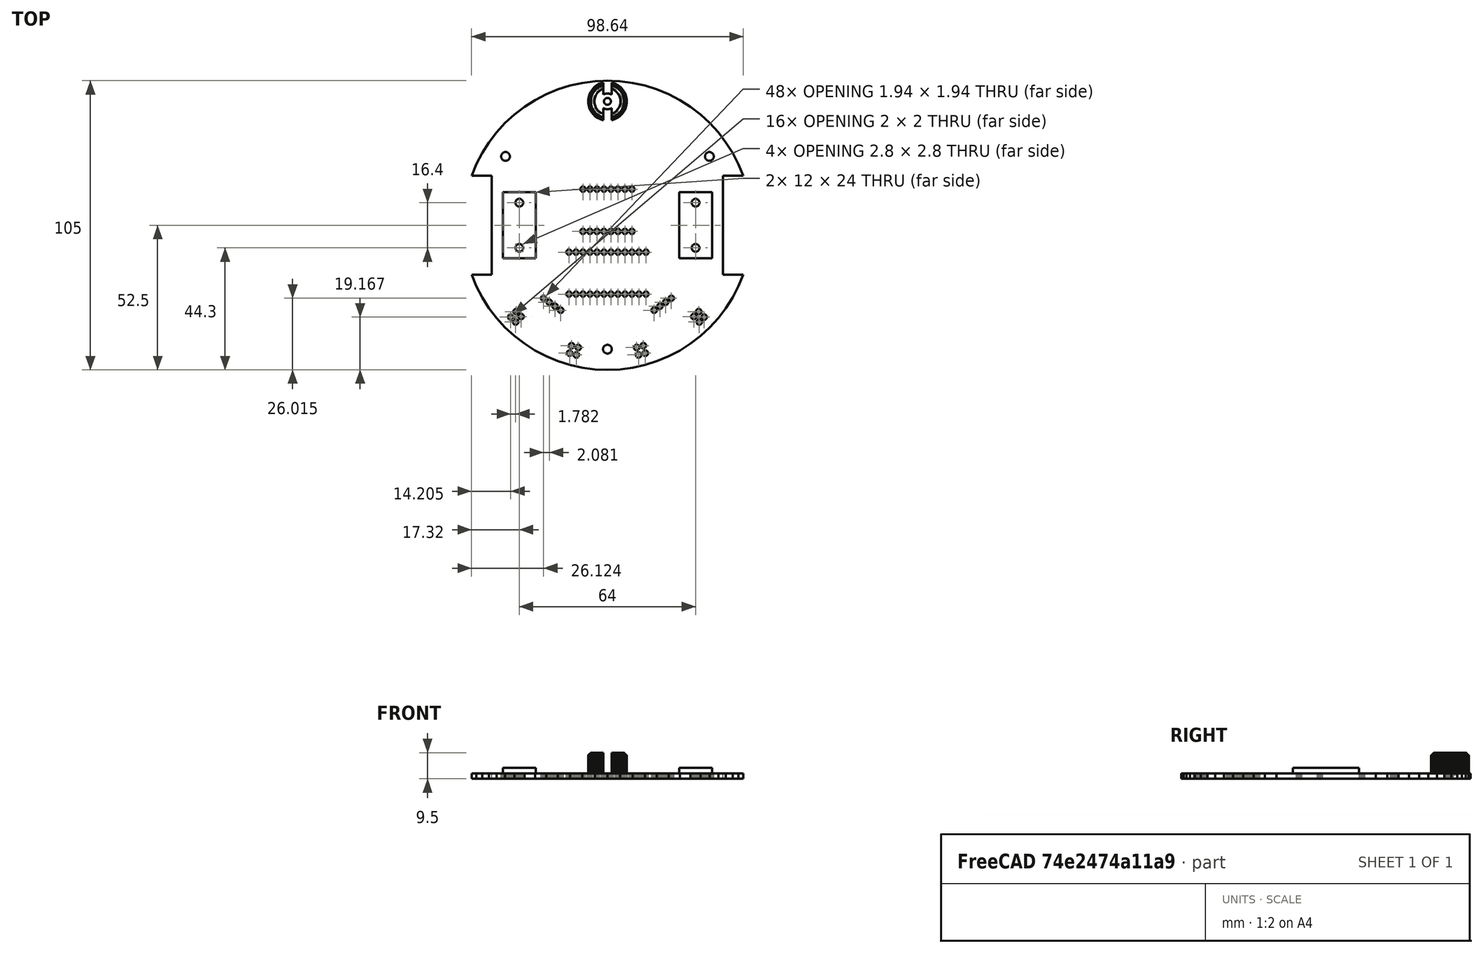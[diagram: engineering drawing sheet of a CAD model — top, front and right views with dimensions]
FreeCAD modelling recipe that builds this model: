
FCSTD DOCUMENT  (FreeCAD 0.17R13522 (Git))
Label: base
License: All rights reserved
LicenseURL: http://en.wikipedia.org/wiki/All_rights_reserved
objects: Part::Prism×75, Part::MultiFuse×14, Part::Box×5, Part::FeaturePython×1, Part::Sphere×1, Part::Cut×1
note: 97 computed .brp shape members not serialized (recipe doc carries the construction recipe); baked Part::Feature solids carry a one-line shape summary decoded from their .brp

FEATURE [Part::Prism] prism
  AttacherType = Attacher::AttachEngine3D
  Circumradius = 52.5
  Height = 2
  Polygon = 72
FEATURE [Part::Prism] prism001
  AttacherType = Attacher::AttachEngine3D
  Circumradius = 7
  Height = 8.5
  Placement = pos=(0,45,0) rot=(0,0,1;0rad)
  Polygon = 72
FEATURE [Part::FeaturePython] frustum  # WARN: FeaturePython — macro-defined, semantics opaque (R4)
  FacesNumber = 72
  Height = 1
  Placement = pos=(0,45,8.5) rot=(0,0,1;0rad)
  Radius1 = 7
  Radius2 = 6
FEATURE [Part::Box] cube
  AttacherType = Attacher::AttachEngine3D
  Height = 4
  Length = 12
  Placement = pos=(-38,-12,0) rot=(0,0,1;0rad)
  Width = 24
FEATURE [Part::Box] cube001
  AttacherType = Attacher::AttachEngine3D
  Height = 4
  Length = 12
  Placement = pos=(26,-12,0) rot=(0,0,1;0rad)
  Width = 24
FEATURE [Part::MultiFuse] union
  Shapes = -> [prism,prism001,frustum,cube,cube001]
FEATURE [Part::Prism] prism002
  AttacherType = Attacher::AttachEngine3D
  Circumradius = 1.25
  Height = 3
  Placement = pos=(0,45,-1) rot=(0,0,1;0rad)
  Polygon = 72
FEATURE [Part::Box] cube002
  AttacherType = Attacher::AttachEngine3D
  Height = 14
  Length = 36
  Placement = pos=(42,-18,-8) rot=(0,0,1;0rad)
  Width = 36
FEATURE [Part::Box] cube003
  AttacherType = Attacher::AttachEngine3D
  Height = 14
  Length = 36
  Placement = pos=(-78,-18,-8) rot=(0,0,1;0rad)
  Width = 36
FEATURE [Part::Prism] prism003
  AttacherType = Attacher::AttachEngine3D
  Circumradius = 1.4
  Height = 15
  Placement = pos=(32,8.2,-1) rot=(0,0,1;0rad)
  Polygon = 72
FEATURE [Part::Prism] prism004
  AttacherType = Attacher::AttachEngine3D
  Circumradius = 1.4
  Height = 15
  Placement = pos=(32,-8.2,-1) rot=(0,0,1;0rad)
  Polygon = 72
FEATURE [Part::Prism] prism005
  AttacherType = Attacher::AttachEngine3D
  Circumradius = 1.4
  Height = 15
  Placement = pos=(-32,8.2,-1) rot=(0,0,1;0rad)
  Polygon = 72
FEATURE [Part::Prism] prism006
  AttacherType = Attacher::AttachEngine3D
  Circumradius = 1.4
  Height = 15
  Placement = pos=(-32,-8.2,-1) rot=(0,0,1;0rad)
  Polygon = 72
FEATURE [Part::Prism] prism007
  AttacherType = Attacher::AttachEngine3D
  Circumradius = 1.6
  Height = 15
  Placement = pos=(37,25,-1) rot=(0,0,1;0rad)
  Polygon = 72
FEATURE [Part::Prism] prism008
  AttacherType = Attacher::AttachEngine3D
  Circumradius = 1.6
  Height = 15
  Placement = pos=(-37,25,-1) rot=(0,0,1;0rad)
  Polygon = 72
FEATURE [Part::Prism] prism009
  AttacherType = Attacher::AttachEngine3D
  Circumradius = 1.6
  Height = 15
  Placement = pos=(0,-45,-1) rot=(0,0,1;0rad)
  Polygon = 72
FEATURE [Part::Prism] prism010
  AttacherType = Attacher::AttachEngine3D
  Circumradius = 1
  Height = 6
  Placement = pos=(1.26,1.4,-3) rot=(0,0,1;0rad)
  Polygon = 72
FEATURE [Part::Prism] prism011
  AttacherType = Attacher::AttachEngine3D
  Circumradius = 1
  Height = 6
  Placement = pos=(-1.26,1.4,-3) rot=(0,0,1;0rad)
  Polygon = 72
FEATURE [Part::Prism] prism012
  AttacherType = Attacher::AttachEngine3D
  Circumradius = 1
  Height = 6
  Placement = pos=(-1.26,-1.4,-3) rot=(0,0,1;0rad)
  Polygon = 72
FEATURE [Part::Prism] prism013
  AttacherType = Attacher::AttachEngine3D
  Circumradius = 1
  Height = 6
  Placement = pos=(1.26,-1.4,-3) rot=(0,0,1;0rad)
  Polygon = 72
FEATURE [Part::MultiFuse] Matrix_Union
  Placement = pos=(-33.234,-33.234,1) rot=(0,0,-1;0.785398rad)
  Shapes = -> [prism010,prism011,prism012,prism013]
FEATURE [Part::Prism] prism014
  AttacherType = Attacher::AttachEngine3D
  Circumradius = 1
  Height = 6
  Placement = pos=(1.26,1.4,-3) rot=(0,0,1;0rad)
  Polygon = 72
FEATURE [Part::Prism] prism015
  AttacherType = Attacher::AttachEngine3D
  Circumradius = 1
  Height = 6
  Placement = pos=(-1.26,1.4,-3) rot=(0,0,1;0rad)
  Polygon = 72
FEATURE [Part::Prism] prism016
  AttacherType = Attacher::AttachEngine3D
  Circumradius = 1
  Height = 6
  Placement = pos=(-1.26,-1.4,-3) rot=(0,0,1;0rad)
  Polygon = 72
FEATURE [Part::Prism] prism017
  AttacherType = Attacher::AttachEngine3D
  Circumradius = 1
  Height = 6
  Placement = pos=(1.26,-1.4,-3) rot=(0,0,1;0rad)
  Polygon = 72
FEATURE [Part::MultiFuse] Matrix_Union001
  Placement = pos=(-12.1645,-45.3985,1) rot=(0,0,-1;0.261799rad)
  Shapes = -> [prism014,prism015,prism016,prism017]
FEATURE [Part::Prism] prism018
  AttacherType = Attacher::AttachEngine3D
  Circumradius = 1
  Height = 6
  Placement = pos=(1.26,1.4,-3) rot=(0,0,1;0rad)
  Polygon = 72
FEATURE [Part::Prism] prism019
  AttacherType = Attacher::AttachEngine3D
  Circumradius = 1
  Height = 6
  Placement = pos=(-1.26,1.4,-3) rot=(0,0,1;0rad)
  Polygon = 72
FEATURE [Part::Prism] prism020
  AttacherType = Attacher::AttachEngine3D
  Circumradius = 1
  Height = 6
  Placement = pos=(-1.26,-1.4,-3) rot=(0,0,1;0rad)
  Polygon = 72
FEATURE [Part::Prism] prism021
  AttacherType = Attacher::AttachEngine3D
  Circumradius = 1
  Height = 6
  Placement = pos=(1.26,-1.4,-3) rot=(0,0,1;0rad)
  Polygon = 72
FEATURE [Part::MultiFuse] Matrix_Union002
  Placement = pos=(12.1645,-45.3985,1) rot=(0,0,1;0.261799rad)
  Shapes = -> [prism018,prism019,prism020,prism021]
FEATURE [Part::Prism] prism022
  AttacherType = Attacher::AttachEngine3D
  Circumradius = 1
  Height = 6
  Placement = pos=(1.26,1.4,-3) rot=(0,0,1;0rad)
  Polygon = 72
FEATURE [Part::Prism] prism023
  AttacherType = Attacher::AttachEngine3D
  Circumradius = 1
  Height = 6
  Placement = pos=(-1.26,1.4,-3) rot=(0,0,1;0rad)
  Polygon = 72
FEATURE [Part::Prism] prism024
  AttacherType = Attacher::AttachEngine3D
  Circumradius = 1
  Height = 6
  Placement = pos=(-1.26,-1.4,-3) rot=(0,0,1;0rad)
  Polygon = 72
FEATURE [Part::Prism] prism025
  AttacherType = Attacher::AttachEngine3D
  Circumradius = 1
  Height = 6
  Placement = pos=(1.26,-1.4,-3) rot=(0,0,1;0rad)
  Polygon = 72
FEATURE [Part::MultiFuse] Matrix_Union003
  Placement = pos=(33.234,-33.234,1) rot=(0,0,1;0.785398rad)
  Shapes = -> [prism022,prism023,prism024,prism025]
FEATURE [Part::MultiFuse] Group
  Shapes = -> [Matrix_Union,Matrix_Union001,Matrix_Union002,Matrix_Union003]
FEATURE [Part::Prism] prism026
  AttacherType = Attacher::AttachEngine3D
  Circumradius = 4.75
  Height = 25
  Placement = pos=(0,45,5.5) rot=(0,0,1;0rad)
  Polygon = 72
FEATURE [Part::Sphere] sphere
  Angle1 = -90
  Angle2 = 90
  Angle3 = 360
  AttacherType = Attacher::AttachEngine3D
  Placement = pos=(0,45,6.4) rot=(0,0,1;0rad)
  Radius = 5.25
FEATURE [Part::Box] cube004
  AttacherType = Attacher::AttachEngine3D
  Height = 16
  Length = 3
  Placement = pos=(-1.5,37.5,2) rot=(0,0,1;0rad)
  Width = 15
FEATURE [Part::Prism] prism027 .. prism034  x8 (patterned run collapsed; names and placements below)
  AttacherType = Attacher::AttachEngine3D
  Circumradius = 0.97
  Height = 10
  Polygon = 72
  placements: 8 in arithmetic series — first pos=(0,0,0) rot=(0,0,1;0rad), step (2.54,0,0), last pos=(17.78,0,0) rot=(0,0,1;0rad)
FEATURE [Part::MultiFuse] Group001
  Placement = pos=(-8.89,22.77,-1) rot=(0,0,1;0rad)
  Shapes = -> [prism027,prism028,prism029,prism030,prism031,prism032,prism033,prism034]
FEATURE [Part::Prism] prism035 .. prism042  x8 (patterned run collapsed; names and placements below)
  AttacherType = Attacher::AttachEngine3D
  Circumradius = 0.97
  Height = 10
  Polygon = 72
  placements: 8 in arithmetic series — first pos=(0,0,0) rot=(0,0,1;0rad), step (2.54,0,0), last pos=(17.78,0,0) rot=(0,0,1;0rad)
FEATURE [Part::MultiFuse] Group002
  Placement = pos=(-8.89,38.1,-1) rot=(0,0,1;0rad)
  Shapes = -> [prism035,prism036,prism037,prism038,prism039,prism040,prism041,prism042]
FEATURE [Part::Prism] prism043 .. prism054  x12 (patterned run collapsed; names and placements below)
  AttacherType = Attacher::AttachEngine3D
  Circumradius = 0.97
  Height = 10
  Polygon = 72
  placements: 12 in arithmetic series — first pos=(0,0,0) rot=(0,0,1;0rad), step (2.54,0,0), last pos=(27.94,0,0) rot=(0,0,1;0rad)
FEATURE [Part::MultiFuse] Group003
  Placement = pos=(-13.97,15.24,-1) rot=(0,0,1;0rad)
  Shapes = -> [prism043,prism044,prism045,prism046,prism047,prism048,prism049,prism050,prism051,prism052,prism053,prism054]
FEATURE [Part::Prism] prism055 .. prism066  x12 (patterned run collapsed; names and placements below)
  AttacherType = Attacher::AttachEngine3D
  Circumradius = 0.97
  Height = 10
  Polygon = 72
  placements: 12 in arithmetic series — first pos=(0,0,0) rot=(0,0,1;0rad), step (2.54,0,0), last pos=(27.94,0,0) rot=(0,0,1;0rad)
FEATURE [Part::MultiFuse] Group004
  Placement = pos=(-13.97,0,-1) rot=(0,0,1;0rad)
  Shapes = -> [prism055,prism056,prism057,prism058,prism059,prism060,prism061,prism062,prism063,prism064,prism065,prism066]
FEATURE [Part::MultiFuse] Matrix_Union004
  Placement = pos=(0,-25,0) rot=(0,0,1;0rad)
  Shapes = -> [Group001,Group002,Group003,Group004]
FEATURE [Part::Prism] prism067 .. prism070  x4 (patterned run collapsed; names and placements below)
  AttacherType = Attacher::AttachEngine3D
  Circumradius = 0.97
  Height = 10
  Polygon = 72
  placements: 4 in arithmetic series — first pos=(0,0,0) rot=(0,0,1;0rad), step (2.54,0,0), last pos=(7.62,0,0) rot=(0,0,1;0rad)
FEATURE [Part::MultiFuse] Group005
  Placement = pos=(16.9542,-30.8556,-1) rot=(0,0,1;0.610865rad)
  Shapes = -> [prism067,prism068,prism069,prism070]
FEATURE [Part::Prism] prism071 .. prism074  x4 (patterned run collapsed; names and placements below)
  AttacherType = Attacher::AttachEngine3D
  Circumradius = 0.97
  Height = 10
  Polygon = 72
  placements: 4 in arithmetic series — first pos=(0,0,0) rot=(0,0,1;0rad), step (2.54,0,0), last pos=(7.62,0,0) rot=(0,0,1;0rad)
FEATURE [Part::MultiFuse] Group006
  Placement = pos=(-23.1961,-26.485,-1) rot=(0,0,-1;0.610865rad)
  Shapes = -> [prism071,prism072,prism073,prism074]
FEATURE [Part::MultiFuse] union001
  Shapes = -> [prism002,cube002,cube003,prism003,prism004,prism005,prism006,prism007,prism008,prism009,Group,prism026,sphere,cube004,Matrix_Union004,Group005,Group006]
FEATURE [Part::Cut] difference
  Base = -> union
  Tool = -> union001
